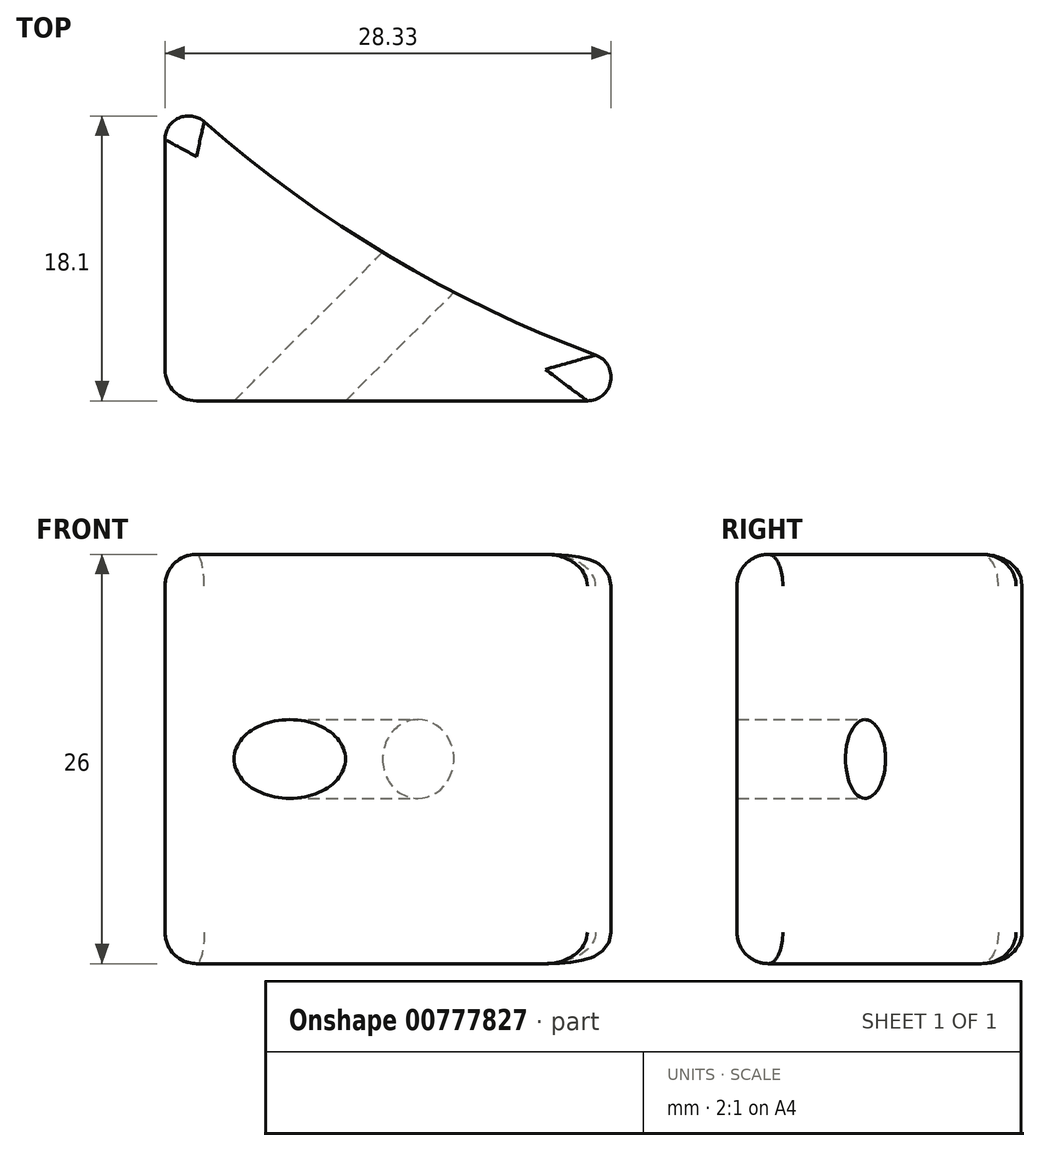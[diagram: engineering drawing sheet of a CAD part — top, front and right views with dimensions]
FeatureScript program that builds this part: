
annotation { "Feature Type Name" : "Feature", "Feature Type Description" : "" }
export const myFeature = defineFeature(function(context is Context, id is Id, definition is map)
    precondition{}
    {
        {
            var Q0;
            Q0=qCreatedBy(makeId("Top.planeOp"),FACE);
            var sketch = newSketch(context, id + "F0", { "sketchPlane" : qUnion([Q0])});
            skLineSegment(sketch, "E0", {"start": v(0, 0) * mm, "end": v(37, 0) * mm});
            skLineSegment(sketch, "E1", {"start": v(0, 0) * mm, "end": v(0, 20) * mm});
            skArc(sketch, "E2", {"start": v(0, 20) * mm, "mid": v(17.16, 7.52) * mm, "end": v(37, 0) * mm});
            skSolve(sketch);
        }
        {
            var Q0;
            Q0 = qSketchRegion(id + "F0", true);
            extrude(context, id + "F1", {"entities" : qUnion([Q0]), "depth" : 26 * mm, "offsetDistance" : 25 * mm});
        }
        {
            var Q0;
            Q0=makeQuery(id+"F1.opExtrude","SWEPT_EDGE",EDGE,{"disambiguationData":[OSD([sQuery(id+"F0.wireOp",EDGE,"E1"),sQuery(id+"F0.wireOp",EDGE,"E2")])]});
            fillet(context, id + "F2", {"entities" : qUnion([Q0]), "radius" : 1.5 * mm, "tangentPropagation" : true, "allowEdgeOverflow" : false});
        }
        {
            var Q0;
            Q0=makeQuery(id+"F1.opExtrude","SWEPT_EDGE",EDGE,{"disambiguationData":[OSD([sQuery(id+"F0.wireOp",EDGE,"E0"),sQuery(id+"F0.wireOp",EDGE,"E2")])]});
            fillet(context, id + "F3", {"entities" : qUnion([Q0]), "radius" : 1.5 * mm, "tangentPropagation" : true, "allowEdgeOverflow" : false});
        }
        {
            var Q0;
            Q0=makeQuery(id+"F1.opExtrude","CAP_EDGE",EDGE,{"disambiguationData":[OSD([sQuery(id+"F0.wireOp",EDGE,"E1")])],"isStart":false});
            fillet(context, id + "F4", {"entities" : qUnion([Q0]), "radius" : 2 * mm, "tangentPropagation" : true, "allowEdgeOverflow" : false});
        }
        {
            var Q0;
            Q0=makeQuery(id+"F1.opExtrude","CAP_EDGE",EDGE,{"disambiguationData":[OSD([sQuery(id+"F0.wireOp",EDGE,"E2")])],"isStart":true});
            fillet(context, id + "F5", {"entities" : qUnion([Q0]), "radius" : 2 * mm, "tangentPropagation" : true, "allowEdgeOverflow" : false});
        }
        {
            var Q0;
            Q0=makeQuery(id+"F1.opExtrude","SWEPT_EDGE",EDGE,{"disambiguationData":[OSD([sQuery(id+"F0.wireOp",EDGE,"E0"),sQuery(id+"F0.wireOp",EDGE,"E1")])]});
            fillet(context, id + "F6", {"entities" : qUnion([Q0]), "radius" : 2 * mm, "tangentPropagation" : true, "allowEdgeOverflow" : false});
        }
        {
            var Q0;
            {var subQ0=sQuery(id+"F0.wireOp",EDGE,"E2");Q0=makeQuery(id+"F3.opFillet","BLEND_EDGE",EDGE,{"blendedFrom":[makeQuery(id+"F1.opExtrude","SWEPT_EDGE",EDGE,{"disambiguationData":[OSD([sQuery(id+"F0.wireOp",EDGE,"E0"),subQ0])]}),makeQuery(id+"F1.opExtrude","SWEPT_FACE",FACE,{"disambiguationData":[OSD([subQ0])]})],"blendedInto":[makeQuery(id+"F1.opExtrude","SWEPT_FACE",FACE,{"disambiguationData":[OSD([subQ0])]})]});}
            cPlane(context, id + "F7", {"entities" : qUnion([Q0]), "cplaneType" : CPlaneType.LINE_ANGLE, "offset" : 25 * mm, "angle" : 315 * degree, "width" : 150 * mm, "height" : 150 * mm});
        }
        {
            var Q0;
            Q0=qCreatedBy(id+"F7.planeOp",FACE);
            var sketch = newSketch(context, id + "F8", { "sketchPlane" : qUnion([Q0])});
            skCircle(sketch, "E3", {"center": v(5.6, 13) * mm, "radius": 2.5 * mm});
            skSolve(sketch);
        }
        {
            var Q0;
            Q0 = qSketchRegion(id + "F8", true);
            extrude(context, id + "F9", {"entities" : qUnion([Q0]), "operationType" : NewBodyOperationType.REMOVE, "depth" : 25 * mm, "offsetDistance" : 25 * mm});
        }
    });
